# Revit family: Blucher_PlumbingFixture_IndustrialDrains_HighFlow_BAa
name_source: partatom
category: Plumbing Fixtures
revit_build: Autodesk Revit 2017 (Build: 20190508_0315(x64)
units: mm (PartAtom-declared; Revit-internal decimal feet)

## family parameters
Cut with Voids When Loaded = No
Host = Face
OmniClass Number = 23.70.50.21.24
OmniClass Title = Waste Water Drains
Part Type = Normal
Room Calculation Point = No
Round Connector Dimension = Use Diameter
Shared = No

## types (16) — shared parameters
Assembly Code = D2030300
AssetType = Fixed
BIMObjectName = Blucher_PlumbingFixture_IndustrialDrains_HighFlow_BA
CW Connection = No
ClassificationName = Uniclass2015
ClassificationValue = Pr_65_52_24_24
Color = Stainless Steel
Description = BA High Flow Industrial Drains - Floor: concrete, tiled and resin
DocumentationCertificates = https://www.bimstore.co
DocumentationInstallationGuide = https://www.bimstore.co
DocumentationInstallationVideo = http://www.blucher.com
DocumentationLiterature = https://www.bimstore.co
DocumentationMaintenance = https://www.bimstore.co
DocumentationTechnical = https://www.bimstore.co
DurationUnit = Years
ExpectedLife = 50
FilterBasket = FB : Filter Basket
Finish = 2B - Pickled
Grade = AISI 304/EN 1.4301 or AISI 316L/EN 1.4404
Grating_696.223 = G : 696.223
Grating_697.225 = G : 697.225
HW Connection = No
IfcExportAs = IfcFlowTerminal
IfcExportType = IfcWasteTerminalTypeEnum.FLOORWASTE
Keynote = R10
Manufacturer = BLÜCHER
ManufacturerName = BLÜCHER
Material = Available in Stainless Steel AISI 304 & Stainless Steel AISI 316L
Model = BA High Flow Industrial Drains
ModelReference = BA High Flow Industrial Drains
NBSDescription = Drainage channels with gratings
NBSObjectName = BLÜCHER - Drainage channels with gratings
NBSReference = 90-05-20/422
ProductionYear = 2019
ReferencedStandard = EN1253
Shape = Square
URL = http://www.blucher.com
Vent Connection = No
WarrantyDurationUnit = Years
Waste Connection = Yes
_BSBibleVersion = 15
_CurrentRevision = 1
_DistributedBy = www.bimstore.co.uk
zero-valued in all types: Default Elevation, HeightFromLevel, _BimSpecGuid

## per-type parameters (varying)
| type | Angle2 | D | D1 | F | F1 | Flow | Flow_Sewer | GratingLength | GratingWidth | H1 | H2 | H3 | H4 | Horizontal | HorizontalOutletLength | NominalDepth | NominalLength | Size | Vertical | aCalc |
| BA400V160 | 90.00° | 160 mm  [stored 0.524934 ft] | 404 mm  [stored 1.32546 ft] | 440 mm  [stored 1.44357 ft] | 440 mm  [stored 1.44357 ft] | 30.0 L/s | 30.0 L/s | 400 mm  [stored 1.31234 ft] | 400 mm  [stored 1.31234 ft] | 60 mm  [stored 0.19685 ft] | 600 mm | 90 mm  [stored 0.295276 ft] | 530 mm  [stored 1.73885 ft] | No | 90 mm  [stored 0.295276 ft] | 440 mm  [stored 1.44357 ft] | 440 mm  [stored 1.44357 ft] | 440 x 440 | Yes | 13 mm  [stored 0.0426509 ft] |
| BA400V200 | 90.00° | 200 mm  [stored 0.656168 ft] | 404 mm  [stored 1.32546 ft] | 440 mm  [stored 1.44357 ft] | 440 mm  [stored 1.44357 ft] | 30.0 L/s | 30.0 L/s | 400 mm  [stored 1.31234 ft] | 400 mm  [stored 1.31234 ft] | 60 mm  [stored 0.19685 ft] | 600 mm | 90 mm  [stored 0.295276 ft] | 530 mm  [stored 1.73885 ft] | No | 90 mm  [stored 0.295276 ft] | 440 mm  [stored 1.44357 ft] | 440 mm  [stored 1.44357 ft] | 440 x 440 | Yes | 13 mm  [stored 0.0426509 ft] |
| BA500V160 | 90.00° | 160 mm  [stored 0.524934 ft] | 504 mm  [stored 1.65354 ft] | 540 mm  [stored 1.77165 ft] | 540 mm  [stored 1.77165 ft] | 45.0 L/s | 45.0 L/s | 500 mm  [stored 1.64042 ft] | 500 mm  [stored 1.64042 ft] | 60 mm  [stored 0.19685 ft] | 800 mm  [stored 2.62467 ft] | 90 mm  [stored 0.295276 ft] | 780 mm  [stored 2.55906 ft] | No | 90 mm  [stored 0.295276 ft] | 540 mm  [stored 1.77165 ft] | 540 mm  [stored 1.77165 ft] | 540 x 540 | Yes | 15 mm  [stored 0.0492126 ft] |
| BA500V200 | 90.00° | 200 mm  [stored 0.656168 ft] | 504 mm  [stored 1.65354 ft] | 540 mm  [stored 1.77165 ft] | 540 mm  [stored 1.77165 ft] | 45.0 L/s | 45.0 L/s | 500 mm  [stored 1.64042 ft] | 500 mm  [stored 1.64042 ft] | 60 mm  [stored 0.19685 ft] | 800 mm  [stored 2.62467 ft] | 90 mm  [stored 0.295276 ft] | 780 mm  [stored 2.55906 ft] | No | 90 mm  [stored 0.295276 ft] | 540 mm  [stored 1.77165 ft] | 540 mm  [stored 1.77165 ft] | 540 x 540 | Yes | 15 mm  [stored 0.0492126 ft] |
| BA500V250 | 90.00° | 250 mm  [stored 0.82021 ft] | 504 mm  [stored 1.65354 ft] | 540 mm  [stored 1.77165 ft] | 540 mm  [stored 1.77165 ft] | 45.0 L/s | 45.0 L/s | 500 mm  [stored 1.64042 ft] | 500 mm  [stored 1.64042 ft] | 60 mm  [stored 0.19685 ft] | 800 mm  [stored 2.62467 ft] | 125 mm  [stored 0.410105 ft] | 780 mm  [stored 2.55906 ft] | No | 125 mm  [stored 0.410105 ft] | 540 mm  [stored 1.77165 ft] | 540 mm  [stored 1.77165 ft] | 540 x 540 | Yes | 16 mm |
| BA800V250 | 90.00° | 250 mm  [stored 0.82021 ft] | 725 mm  [stored 2.37861 ft] | 840 mm  [stored 2.75591 ft] | 840 mm  [stored 2.75591 ft] | 60.0 L/s | 60.0 L/s | 800 mm  [stored 2.62467 ft] | 800 mm  [stored 2.62467 ft] | 80 mm  [stored 0.262467 ft] | 1200 mm | 125 mm  [stored 0.410105 ft] | 1070 mm  [stored 3.5105 ft] | No | 125 mm  [stored 0.410105 ft] | 840 mm  [stored 2.75591 ft] | 840 mm  [stored 2.75591 ft] | 840 x 840 | Yes | 21 mm |
| BA800V315 | 90.00° | 315 mm  [stored 1.03346 ft] | 725 mm  [stored 2.37861 ft] | 840 mm  [stored 2.75591 ft] | 840 mm  [stored 2.75591 ft] | 60.0 L/s | 60.0 L/s | 800 mm  [stored 2.62467 ft] | 800 mm  [stored 2.62467 ft] | 80 mm  [stored 0.262467 ft] | 1200 mm | 125 mm  [stored 0.410105 ft] | 1070 mm  [stored 3.5105 ft] | No | 125 mm  [stored 0.410105 ft] | 840 mm  [stored 2.75591 ft] | 840 mm  [stored 2.75591 ft] | 840 x 840 | Yes | 21 mm |
| BA400H160 | 2.50° | 160 mm  [stored 0.524934 ft] | 404 mm  [stored 1.32546 ft] | 440 mm  [stored 1.44357 ft] | 440 mm  [stored 1.44357 ft] | 30.0 L/s | 30.0 L/s | 400 mm  [stored 1.31234 ft] | 400 mm  [stored 1.31234 ft] | 60 mm  [stored 0.19685 ft] | 600 mm | 90 mm  [stored 0.295276 ft] | 530 mm  [stored 1.73885 ft] | Yes | 292 mm  [stored 0.958005 ft] | 440 mm  [stored 1.44357 ft] | 440 mm  [stored 1.44357 ft] | 440 x 440 | No | 13 mm  [stored 0.0426509 ft] |
| BA400H200 | 2.50° | 200 mm  [stored 0.656168 ft] | 404 mm  [stored 1.32546 ft] | 440 mm  [stored 1.44357 ft] | 440 mm  [stored 1.44357 ft] | 30.0 L/s | 30.0 L/s | 400 mm  [stored 1.31234 ft] | 400 mm  [stored 1.31234 ft] | 60 mm  [stored 0.19685 ft] | 600 mm | 90 mm  [stored 0.295276 ft] | 530 mm  [stored 1.73885 ft] | Yes | 292 mm  [stored 0.958005 ft] | 440 mm  [stored 1.44357 ft] | 440 mm  [stored 1.44357 ft] | 440 x 440 | No | 13 mm  [stored 0.0426509 ft] |
| BA500H160 | 2.50° | 160 mm  [stored 0.524934 ft] | 504 mm  [stored 1.65354 ft] | 540 mm  [stored 1.77165 ft] | 540 mm  [stored 1.77165 ft] | 45.0 L/s | 45.0 L/s | 500 mm  [stored 1.64042 ft] | 500 mm  [stored 1.64042 ft] | 60 mm  [stored 0.19685 ft] | 800 mm  [stored 2.62467 ft] | 90 mm  [stored 0.295276 ft] | 780 mm  [stored 2.55906 ft] | Yes | 342 mm  [stored 1.12205 ft] | 540 mm  [stored 1.77165 ft] | 540 mm  [stored 1.77165 ft] | 540 x 540 | No | 15 mm  [stored 0.0492126 ft] |
| BA500H200 | 2.50° | 200 mm  [stored 0.656168 ft] | 504 mm  [stored 1.65354 ft] | 540 mm  [stored 1.77165 ft] | 540 mm  [stored 1.77165 ft] | 45.0 L/s | 45.0 L/s | 500 mm  [stored 1.64042 ft] | 500 mm  [stored 1.64042 ft] | 60 mm  [stored 0.19685 ft] | 800 mm  [stored 2.62467 ft] | 90 mm  [stored 0.295276 ft] | 780 mm  [stored 2.55906 ft] | Yes | 342 mm  [stored 1.12205 ft] | 540 mm  [stored 1.77165 ft] | 540 mm  [stored 1.77165 ft] | 540 x 540 | No | 15 mm  [stored 0.0492126 ft] |
| BA500H250 | 2.50° | 250 mm  [stored 0.82021 ft] | 504 mm  [stored 1.65354 ft] | 540 mm  [stored 1.77165 ft] | 540 mm  [stored 1.77165 ft] | 45.0 L/s | 45.0 L/s | 500 mm  [stored 1.64042 ft] | 500 mm  [stored 1.64042 ft] | 60 mm  [stored 0.19685 ft] | 800 mm  [stored 2.62467 ft] | 125 mm  [stored 0.410105 ft] | 780 mm  [stored 2.55906 ft] | Yes | 377 mm  [stored 1.23688 ft] | 540 mm  [stored 1.77165 ft] | 540 mm  [stored 1.77165 ft] | 540 x 540 | No | 16 mm |
| BA800H250 | 2.50° | 250 mm  [stored 0.82021 ft] | 725 mm  [stored 2.37861 ft] | 840 mm  [stored 2.75591 ft] | 840 mm  [stored 2.75591 ft] | 60.0 L/s | 60.0 L/s | 800 mm  [stored 2.62467 ft] | 800 mm  [stored 2.62467 ft] | 80 mm  [stored 0.262467 ft] | 1200 mm | 125 mm  [stored 0.410105 ft] | 1070 mm  [stored 3.5105 ft] | Yes | 488 mm | 840 mm  [stored 2.75591 ft] | 840 mm  [stored 2.75591 ft] | 840 x 840 | No | 21 mm |
| BA800H315 | 2.50° | 315 mm  [stored 1.03346 ft] | 725 mm  [stored 2.37861 ft] | 840 mm  [stored 2.75591 ft] | 840 mm  [stored 2.75591 ft] | 60.0 L/s | 60.0 L/s | 800 mm  [stored 2.62467 ft] | 800 mm  [stored 2.62467 ft] | 80 mm  [stored 0.262467 ft] | 1200 mm | 125 mm  [stored 0.410105 ft] | 1070 mm  [stored 3.5105 ft] | Yes | 488 mm | 840 mm  [stored 2.75591 ft] | 840 mm  [stored 2.75591 ft] | 840 x 840 | No | 21 mm |
| BA400V250 | 90.00° | 250 mm  [stored 0.82021 ft] | 365 mm  [stored 1.19751 ft] | 440 mm  [stored 1.44357 ft] | 440 mm  [stored 1.44357 ft] | 30.0 L/s | 30.0 L/s | 400 mm  [stored 1.31234 ft] | 400 mm  [stored 1.31234 ft] | 100 mm  [stored 0.328084 ft] | 600 mm | 123 mm  [stored 0.403543 ft] | 530 mm  [stored 1.73885 ft] | No | 123 mm  [stored 0.403543 ft] | 440 mm  [stored 1.44357 ft] | 440 mm  [stored 1.44357 ft] | 440 x 440 | Yes | 13 mm  [stored 0.0426509 ft] |
| BA500V315 | 90.00° | 315 mm  [stored 1.03346 ft] | 465 mm  [stored 1.52559 ft] | 540 mm  [stored 1.77165 ft] | 540 mm  [stored 1.77165 ft] | 45.0 L/s | 45.0 L/s | 500 mm  [stored 1.64042 ft] | 500 mm  [stored 1.64042 ft] | 100 mm  [stored 0.328084 ft] | 800 mm  [stored 2.62467 ft] | 143 mm | 780 mm  [stored 2.55906 ft] | No | 143 mm | 540 mm  [stored 1.77165 ft] | 540 mm  [stored 1.77165 ft] | 540 x 540 | Yes | 16 mm |

note: column(s) folded — value = type name in every type: ChannelProductCode, Type Comments, TypeName

note: [stored X ft] marks values corroborated as IEEE doubles in the binary element streams (Revit-internal decimal feet)

## geometry (parser evidence)
native form markers: Blend x2, Sweep x7
no freeform markers — native parametric forms only
